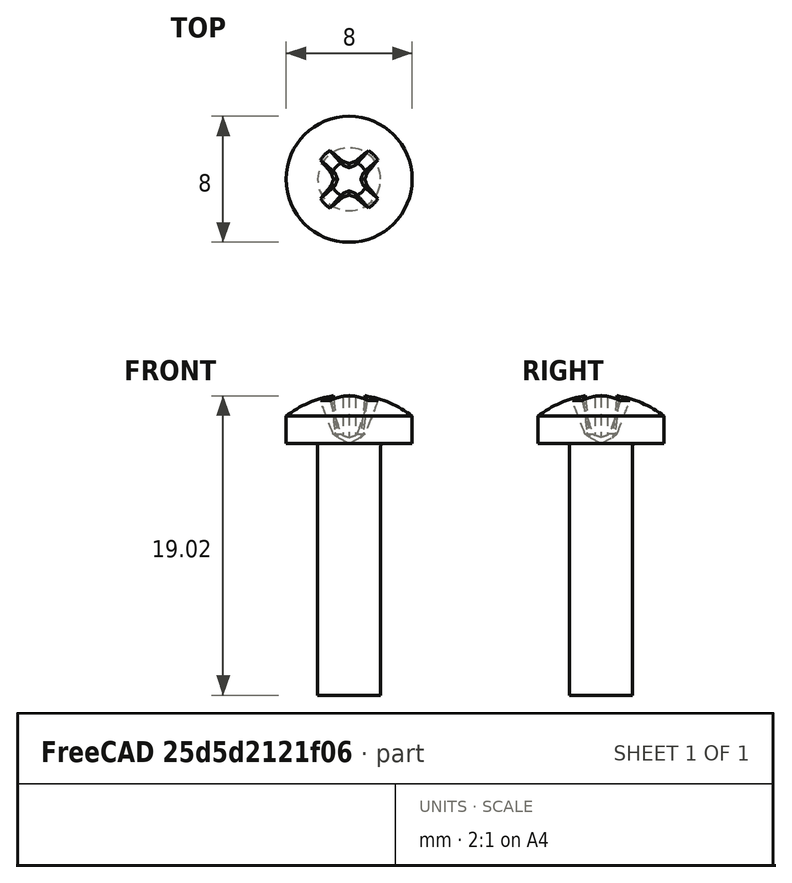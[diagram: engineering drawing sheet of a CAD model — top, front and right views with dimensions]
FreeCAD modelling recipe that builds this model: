
FCSTD DOCUMENT  (FreeCAD 0.19R24367 (Git))
Label: WheelAssembly
License: All rights reserved
LicenseURL: http://en.wikipedia.org/wiki/All_rights_reserved
objects: App::Link×5, PartDesign::CoordinateSystem×3, App::DocumentObjectGroup×3, App::Part×2, App::FeaturePython×1, Part::FeaturePython×1
note: 4 computed .brp shape members not serialized (recipe doc carries the construction recipe); baked Part::Feature solids carry a one-line shape summary decoded from their .brp
EXTERNAL_REF file=parts/Motor.FCStd obj=LCS_1
EXTERNAL_REF file=parts/Motor.FCStd obj=Motor
EXTERNAL_REF file=parts/MotorBracket.FCStd obj=LCS_1
EXTERNAL_REF file=parts/MotorBracket.FCStd obj=Front
EXTERNAL_REF file=parts/Coupling.FCStd obj=LCS_1
EXTERNAL_REF file=parts/Motor.FCStd obj=LCS_2
EXTERNAL_REF file=parts/Coupling.FCStd obj=Coupling
EXTERNAL_REF file=parts/Coupling.FCStd obj=LCS_2
EXTERNAL_REF file=parts/Wheel.FCStd obj=LCS_1
EXTERNAL_REF file=parts/Wheel.FCStd obj=Wheel
EXTERNAL_REF file=parts/Wheel.FCStd obj=LCS_2

FEATURE [PartDesign::CoordinateSystem] LCS_Origin
  AttacherType = Attacher::AttachEngine3D
  MapMode = 2
  Support = -> [X_Axis]
FEATURE [App::FeaturePython] Variables  # WARN: FeaturePython — macro-defined, semantics opaque (R4)
  Type = App::PropertyContainer
FEATURE [App::DocumentObjectGroup] Constraints
FEATURE [App::DocumentObjectGroup] Configurations
FEATURE [App::Link] Motor
  AssemblyType = Part::Link
  AttachedBy = #LCS_1
  AttachedTo = Parent Assembly#LCS_Origin
  AttachmentOffset = pos=(0,0,0) rot=(0,1,0;4.71239rad)
  LinkPlacement = pos=(22,-4.4e-15,4.9e-15) rot=(0,1,0;4.71239rad)
  LinkedObject = -> <external parts/Motor.FCStd>#Motor
  Placement = pos=(22,-4.4e-15,4.9e-15) rot=(0,1,0;4.71239rad)
  SolverId = Asm4EE
  expr: Placement = LCS_Origin.Placement * AttachmentOffset * Motor#LCS_1.Placement ^ -1
FEATURE [App::Link] Front
  AssemblyType = Part::Link
  AttachedBy = #LCS_1
  AttachedTo = Motor#LCS_1
  LinkPlacement = pos=(8,-3e-16,1.8e-15) rot=(0,0.707107,-0.707107;3.14159rad)
  LinkedObject = -> <external parts/MotorBracket.FCStd>#Front
  Placement = pos=(8,-3e-16,1.8e-15) rot=(0,0.707107,-0.707107;3.14159rad)
  SolverId = Asm4EE
  expr: Placement = Motor.Placement * Motor#LCS_1.Placement * AttachmentOffset * MotorBracket#LCS_1.Placement ^ -1
FEATURE [App::Link] Coupling
  AssemblyType = Part::Link
  AttachedBy = #LCS_1
  AttachedTo = Motor#LCS_2
  AttachmentOffset = pos=(0,0,1) rot=(0,0,1;3.14159rad)
  LinkPlacement = pos=(-7,-7,-1.6e-15) rot=(0,1,0;4.71239rad)
  LinkedObject = -> <external parts/Coupling.FCStd>#Coupling
  Placement = pos=(-7,-7,-1.6e-15) rot=(0,1,0;4.71239rad)
  SolverId = Asm4EE
  expr: Placement = Motor.Placement * Motor#LCS_2.Placement * AttachmentOffset * Coupling#LCS_1.Placement ^ -1
FEATURE [App::Link] Wheel
  AssemblyType = Part::Link
  AttachedBy = #LCS_1
  AttachedTo = Coupling#LCS_2
  LinkPlacement = pos=(-47,-7,-1.04e-14) rot=(0,1,0;4.71239rad)
  LinkedObject = -> <external parts/Wheel.FCStd>#Wheel
  Placement = pos=(-47,-7,-1.04e-14) rot=(0,1,0;4.71239rad)
  SolverId = Asm4EE
  expr: Placement = Coupling.Placement * Coupling#LCS_2.Placement * AttachmentOffset * Wheel#LCS_1.Placement ^ -1
FEATURE [Part::FeaturePython] Screw  label="M4x16-Screw"  # Fasteners workbench fastener (typed FeaturePython)
  diameter = 6
  invert = false
  length = 6
  lengthCustom = 16
  matchOuter = false
  offset = 0
  thread = false
  type = 34
FEATURE [PartDesign::CoordinateSystem] LCS_0
  AttacherType = Attacher::AttachEngine3D
  MapMode = 2
  Support = -> [X_Axis001]
FEATURE [PartDesign::CoordinateSystem] LCS_1
  AttacherType = Attacher::AttachEngine3D
  MapMode = 5
  Placement = pos=(0,0,0) rot=(0,0,1;3.14159rad)
  Support = -> [Screw]
FEATURE [App::Part] Screw001
  Group = -> [LCS_0,Screw,LCS_1]
  Origin = -> Origin001
FEATURE [App::DocumentObjectGroup] Parts
  Group = -> [Screw001]
FEATURE [App::Link] Screw001001
  AssemblyType = Part::Link
  AttachedBy = #LCS_1
  AttachedTo = Wheel#LCS_2
  LinkPlacement = pos=(-54,-7,-1.2e-14) rot=(0,1,0;4.71239rad)
  LinkedObject = -> Screw001
  Placement = pos=(-54,-7,-1.2e-14) rot=(0,1,0;4.71239rad)
  SolverId = Asm4EE
  expr: Placement = Wheel.Placement * Wheel#LCS_2.Placement * AttachmentOffset * LCS_1.Placement ^ -1
FEATURE [App::Part] Assembly  label="WheelAssembly"
  AssemblyType = Part::Link
  Group = -> [LCS_Origin,Variables,Constraints,Configurations,Motor,Front,Coupling,Wheel,Screw001001]
  Origin = -> Origin
  Type = Assembly

RESOLVED EXTERNAL PARTS (link-assembly join: the EXTERNAL_REF files above that resolve inside this repo's crawl, each included once):
---- part parts/Coupling.FCStd = doc fcstd_91e699eaf496 ----
FCSTD DOCUMENT  (FreeCAD 0.19R24367 (Git))
Label: Coupling
License: All rights reserved
LicenseURL: http://en.wikipedia.org/wiki/All_rights_reserved
objects: Sketcher::SketchObject×5, PartDesign::CoordinateSystem×3, PartDesign::Pad×2, PartDesign::Pocket×2, PartDesign::Hole×1, PartDesign::Plane×1, PartDesign::Body×1, App::Part×1
note: 20 computed .brp shape members not serialized (recipe doc carries the construction recipe); baked Part::Feature solids carry a one-line shape summary decoded from their .brp

FEATURE [PartDesign::CoordinateSystem] LCS_0
  AttacherType = Attacher::AttachEngine3D
  MapMode = 2
  Support = -> [X_Axis]
FEATURE [Sketcher::SketchObject] Sketch
  FullyConstrained = true
  MapMode = 5
  Support = -> [XY_Plane001]
  sketch-geometry (1):
    g0: Circle CenterX=0 CenterY=0 CenterZ=0 NormalX=0 NormalY=0 NormalZ=1 AngleXU=0 Radius=6
  constraints (2):
    c: Coincident(g0,g-1)
    c: Diameter(g0) = 12
FEATURE [PartDesign::Pad] Pad
  Direction = (1,1,1)
  Length = 30
  Length2 = 100
  Profile = -> Sketch
  Type = 0
FEATURE [Sketcher::SketchObject] Sketch001
  FullyConstrained = true
  MapMode = 5
  Placement = pos=(0,0,30) rot=(0,0,1;0rad)
  Support = -> [Pad]
  sketch-geometry (8):
    g0: LineSegment StartX=6.49519 StartY=-3.75 StartZ=0 EndX=6.49519 EndY=3.75 EndZ=0
    g1: LineSegment StartX=6.49519 StartY=3.75 StartZ=0 EndX=9e-16 EndY=7.5 EndZ=0
    g2: LineSegment StartX=9e-16 StartY=7.5 StartZ=0 EndX=-6.49519 EndY=3.75 EndZ=0
    g3: LineSegment StartX=-6.49519 StartY=3.75 StartZ=0 EndX=-6.49519 EndY=-3.75 EndZ=0
    g4: LineSegment StartX=-6.49519 StartY=-3.75 StartZ=0 EndX=0 EndY=-7.5 EndZ=0
    g5: LineSegment StartX=0 StartY=-7.5 StartZ=0 EndX=6.49519 EndY=-3.75 EndZ=0
    g6: Circle CenterX=0 CenterY=0 CenterZ=0 NormalX=0 NormalY=0 NormalZ=1 AngleXU=0 Radius=7.5
    g7: LineSegment StartX=0 StartY=0 StartZ=0 EndX=6.49519 EndY=0 EndZ=0
  constraints (19):
    c: Coincident(g0,g1)
    c: Coincident(g1,g2)
    c: Coincident(g2,g3)
    c: Coincident(g3,g4)
    c: Coincident(g4,g5)
    c: Coincident(g5,g0)
    c: Equal(g0, g1-g5) x5
    c: PointOnObject(g0,g6)
    c: PointOnObject(g1,g6)
    c: PointOnObject(g2,g6)
    c: PointOnObject(g3,g6)
    c: PointOnObject(g4,g6)
    c: PointOnObject(g5,g6)
    c: Coincident(g6,g-1)
    c: PointOnObject(g4,g-2)
    c: Coincident(g7,g-1)
    c: PointOnObject(g7,g-1)
    c: PointOnObject(g7,g0)
    c: Diameter(g6) = 15
FEATURE [PartDesign::Pad] Pad001
  BaseFeature = -> Pad
  Direction = (1,1,1)
  Length = 10
  Length2 = 100
  Profile = -> Sketch001
  Reversed = true
  Type = 0
FEATURE [Sketcher::SketchObject] Sketch002
  FullyConstrained = true
  MapMode = 5
  Placement = pos=(0,0,30) rot=(0,0,1;0rad)
  Support = -> [Pad001]
  sketch-geometry (1):
    g0: Circle CenterX=0 CenterY=0 CenterZ=0 NormalX=0 NormalY=0 NormalZ=1 AngleXU=0 Radius=2
  constraints (2):
    c: Coincident(g0,g-1)
    c: Diameter(g0) = 4
FEATURE [PartDesign::Hole] Hole
  BaseFeature = -> Pad001
  Depth = 5
  DepthType = 0
  Diameter = 3.5
  DrillForDepth = false
  DrillPoint = 1
  DrillPointAngle = 118
  HoleCutCountersinkAngle = 90
  HoleCutCustomValues = false
  HoleCutDepth = 0
  HoleCutDiameter = 6.1
  HoleCutType = 0
  ModelActualThread = false
  Profile = -> Sketch002
  Tapered = false
  TaperedAngle = 90
  ThreadAngle = 60
  ThreadClass = 0
  ThreadCutOffInner = 0.0541266
  ThreadCutOffOuter = 0.108253
  ThreadDirection = 0
  ThreadFit = 0
  ThreadPitch = 0.5
  ThreadSize = 11
  ThreadType = 2
  Threaded = true
FEATURE [Sketcher::SketchObject] Sketch003
  FullyConstrained = true
  MapMode = 5
  Placement = pos=(0,0,0) rot=(1,0,0;3.14159rad)
  Support = -> [Hole]
  sketch-geometry (1):
    g0: Circle CenterX=0 CenterY=0 CenterZ=0 NormalX=0 NormalY=0 NormalZ=1 AngleXU=0 Radius=3
  constraints (2):
    c: Coincident(g0,g-1)
    c: Diameter(g0) = 6
FEATURE [PartDesign::Pocket] Pocket
  BaseFeature = -> Hole
  Length = 15
  Length2 = 100
  Profile = -> Sketch003
  Type = 0
FEATURE [PartDesign::Plane] DatumPlane
  AttachmentOffset = pos=(0,6,0) rot=(1,0,0;1.5708rad)
  Length = 60
  MapMode = 45
  Placement = pos=(-1.8e-15,6,10) rot=(1,0,0;1.5708rad)
  ResizeMode = 0
  Support = -> [Pocket]
  Width = 60
FEATURE [Sketcher::SketchObject] Sketch004
  FullyConstrained = true
  MapMode = 5
  Placement = pos=(-1.8e-15,6,10) rot=(1,0,0;1.5708rad)
  Support = -> [DatumPlane]
  sketch-geometry (1):
    g0: Circle CenterX=0 CenterY=-5 CenterZ=0 NormalX=0 NormalY=0 NormalZ=1 AngleXU=0 Radius=2
  constraints (3):
    c: PointOnObject(g0,g-2)
    c: Diameter(g0) = 4
    c: DistanceY(g0,g-1) = 5
FEATURE [PartDesign::Pocket] Pocket001
  BaseFeature = -> Pocket
  Length = 5
  Length2 = 100
  Profile = -> Sketch004
  Refine = true
  Reversed = true
  Type = 0
FEATURE [PartDesign::Body] Body
  Group = -> [Sketch,Pad,Sketch001,Pad001,Sketch002,Hole,Sketch003,Pocket,DatumPlane,Sketch004,Pocket001]
  Origin = -> Origin001
  Tip = -> Pocket001
FEATURE [PartDesign::CoordinateSystem] LCS_1
  AttacherType = Attacher::AttachEngine3D
  MapMode = 5
  Placement = pos=(0,0,0) rot=(0,0,1;3.14159rad)
  Support = -> [Pocket001]
FEATURE [PartDesign::CoordinateSystem] LCS_2
  AttacherType = Attacher::AttachEngine3D
  MapMode = 5
  Placement = pos=(0,0,20) rot=(0,0,1;3.14159rad)
  Support = -> [Pocket001]
FEATURE [App::Part] Coupling
  Group = -> [LCS_0,Body,LCS_1,LCS_2]
  Origin = -> Origin
---- part parts/Motor.FCStd = doc fcstd_aef168587a4c ----
FCSTD DOCUMENT  (FreeCAD 0.19R24367 (Git))
Label: Motor
License: All rights reserved
LicenseURL: http://en.wikipedia.org/wiki/All_rights_reserved
objects: Sketcher::SketchObject×9, PartDesign::Pad×6, PartDesign::Fillet×6, PartDesign::Pocket×2, PartDesign::CoordinateSystem×2, PartDesign::PolarPattern×1, PartDesign::Chamfer×1, PartDesign::Revolution×1, PartDesign::Body×1, App::Part×1
note: 45 computed .brp shape members not serialized (recipe doc carries the construction recipe); baked Part::Feature solids carry a one-line shape summary decoded from their .brp

FEATURE [Sketcher::SketchObject] Sketch
  FullyConstrained = true
  MapMode = 5
  Support = -> [XY_Plane]
  sketch-geometry (1):
    g0: Circle CenterX=0 CenterY=0 CenterZ=0 NormalX=0 NormalY=0 NormalZ=1 AngleXU=0 Radius=18.5
  constraints (2):
    c: Coincident(g0,g-1)
    c: Diameter(g0) = 37
FEATURE [PartDesign::Pad] Pad
  Direction = (1,1,1)
  Length = 22
  Length2 = 100
  Profile = -> Sketch
  Type = 0
FEATURE [Sketcher::SketchObject] Sketch001
  FullyConstrained = true
  MapMode = 5
  Placement = pos=(0,0,22) rot=(0,0,1;0rad)
  Support = -> [Pad]
  sketch-geometry (3):
    g0: Circle CenterX=0 CenterY=0 CenterZ=0 NormalX=0 NormalY=0 NormalZ=1 AngleXU=0 Radius=15.5
    g1: LineSegment StartX=0 StartY=0 StartZ=0 EndX=7.75 EndY=13.4234 EndZ=0
    g2: Circle CenterX=7.75 CenterY=13.4234 CenterZ=0 NormalX=0 NormalY=0 NormalZ=1 AngleXU=0 Radius=1.5
  constraints (8):
    c: Coincident(g0,g-1)
    c: Diameter(g0) = 31
    c: Coincident(g1,g-1)
    c: PointOnObject(g1,g0)
    c: Distance(g1) = 15.5
    c: Angle(g1,g-2) = 0.523599
    c: Coincident(g2,g1)
    c: Diameter(g2) = 3
FEATURE [PartDesign::Pocket] Pocket
  BaseFeature = -> Pad
  Length = 5
  Length2 = 100
  Profile = -> Sketch001
  Type = 0
FEATURE [PartDesign::PolarPattern] PolarPattern
  Angle = 360
  Axis = -> Sketch001 [N_Axis]
  BaseFeature = -> Pocket
  Occurrences = 6
  Originals = -> [Pocket]
FEATURE [Sketcher::SketchObject] Sketch002
  FullyConstrained = true
  MapMode = 5
  Placement = pos=(0,0,22) rot=(0,0,1;0rad)
  Support = -> [PolarPattern]
  sketch-geometry (1):
    g0: Circle CenterX=0 CenterY=7 CenterZ=0 NormalX=0 NormalY=0 NormalZ=1 AngleXU=0 Radius=6
  constraints (3):
    c: PointOnObject(g0,g-2)
    c: Diameter(g0) = 12
    c: DistanceY(g-1,g0) = 7
FEATURE [PartDesign::Pad] Pad001
  BaseFeature = -> PolarPattern
  Direction = (1,1,1)
  Length = 6
  Length2 = 100
  Profile = -> Sketch002
  Type = 0
FEATURE [Sketcher::SketchObject] Sketch003
  FullyConstrained = true
  MapMode = 5
  Placement = pos=(0,0,28) rot=(0,0,1;0rad)
  Support = -> [Pad001]
  sketch-geometry (1):
    g0: Circle CenterX=0 CenterY=7 CenterZ=0 NormalX=0 NormalY=0 NormalZ=1 AngleXU=0 Radius=3
  constraints (3):
    c: PointOnObject(g0,g-2)
    c: Diameter(g0) = 6
    c: DistanceY(g-1,g0) = 7
FEATURE [PartDesign::Pad] Pad002
  BaseFeature = -> Pad001
  Direction = (1,1,1)
  Length = 15.5
  Length2 = 100
  Profile = -> Sketch003
  Type = 0
FEATURE [Sketcher::SketchObject] Sketch004
  FullyConstrained = true
  MapMode = 5
  Placement = pos=(0,0,43.5) rot=(0,0,1;0rad)
  Support = -> [Pad002]
  sketch-geometry (4):
    g0: LineSegment StartX=-1.7 StartY=4.5 StartZ=0 EndX=1.7 EndY=4.5 EndZ=0
    g1: LineSegment StartX=1.7 StartY=4.5 StartZ=0 EndX=1.7 EndY=4 EndZ=0
    g2: LineSegment StartX=1.7 StartY=4 StartZ=0 EndX=-1.7 EndY=4 EndZ=0
    g3: LineSegment StartX=-1.7 StartY=4 StartZ=0 EndX=-1.7 EndY=4.5 EndZ=0
  constraints (11):
    c: Coincident(g0,g1)
    c: Coincident(g1,g2)
    c: Coincident(g2,g3)
    c: Coincident(g3,g0)
    c: Horizontal(g2)
    c: Vertical(g1)
    c: Vertical(g3)
    c: Symmetric(g0,g0,g-2)
    c: Distance(g1) = 0.5
    c: DistanceY(g-1,g1) = 4
    c: Distance(g0) = 3.4
FEATURE [PartDesign::Pocket] Pocket001
  BaseFeature = -> Pad002
  Length = 12
  Length2 = 100
  Profile = -> Sketch004
  Type = 0
FEATURE [PartDesign::Fillet] Fillet
  Base = -> Pocket001 [Edge3]
  BaseFeature = -> Pocket001
  Radius = 0.5
  SupportTransform = false
FEATURE [PartDesign::Fillet] Fillet001
  Base = -> Fillet [Edge22]
  BaseFeature = -> Fillet
  Radius = 1
  SupportTransform = false
FEATURE [PartDesign::Fillet] Fillet002
  Base = -> Fillet001 [Face20]
  BaseFeature = -> Fillet001
  Radius = 0.5
  SupportTransform = false
FEATURE [PartDesign::Fillet] Fillet003
  Base = -> Fillet002 [Edge46]
  BaseFeature = -> Fillet002
  Radius = 0.5
  SupportTransform = false
FEATURE [Sketcher::SketchObject] Sketch005
  FullyConstrained = true
  MapMode = 5
  Placement = pos=(0,0,0) rot=(1,0,0;3.14159rad)
  Support = -> [Fillet003]
  sketch-geometry (1):
    g0: Circle CenterX=0 CenterY=0 CenterZ=0 NormalX=0 NormalY=0 NormalZ=1 AngleXU=0 Radius=18
  constraints (2):
    c: Coincident(g0,g-1)
    c: Diameter(g0) = 36
FEATURE [PartDesign::Pad] Pad003
  BaseFeature = -> Fillet003
  Direction = (1,1,1)
  Length = 50
  Length2 = 100
  Profile = -> Sketch005
  Type = 0
FEATURE [Sketcher::SketchObject] Sketch006
  FullyConstrained = true
  MapMode = 5
  Placement = pos=(0,0,-50) rot=(1,0,0;3.14159rad)
  Support = -> [Pad003]
  sketch-geometry (1):
    g0: Circle CenterX=0 CenterY=0 CenterZ=0 NormalX=0 NormalY=0 NormalZ=1 AngleXU=0 Radius=6.5
  constraints (2):
    c: Coincident(g0,g-1)
    c: Diameter(g0) = 13
FEATURE [PartDesign::Pad] Pad004
  BaseFeature = -> Pad003
  Direction = (1,1,1)
  Length = 4
  Length2 = 100
  Profile = -> Sketch006
  Type = 0
FEATURE [PartDesign::Chamfer] Chamfer
  Angle = 45
  Base = -> Pad004 [Edge33]
  BaseFeature = -> Pad004
  ChamferType = 0
  FlipDirection = false
  Size = 2
  Size2 = 1
  SupportTransform = false
FEATURE [Sketcher::SketchObject] Sketch007
  FullyConstrained = true
  MapMode = 5
  Placement = pos=(0,0,-54) rot=(1,0,0;3.14159rad)
  Support = -> [Chamfer]
  sketch-geometry (1):
    g0: Circle CenterX=0 CenterY=0 CenterZ=0 NormalX=0 NormalY=0 NormalZ=1 AngleXU=0 Radius=1.5
  constraints (2):
    c: Coincident(g0,g-1)
    c: Diameter(g0) = 3
FEATURE [PartDesign::Pad] Pad005
  BaseFeature = -> Chamfer
  Direction = (1,1,1)
  Length = 3
  Length2 = 100
  Profile = -> Sketch007
  Type = 0
FEATURE [PartDesign::Fillet] Fillet004
  Base = -> Pad005 [Face8]
  BaseFeature = -> Pad005
  Radius = 0.5
  SupportTransform = false
FEATURE [PartDesign::Fillet] Fillet005
  Base = -> Fillet004 [Edge11]
  BaseFeature = -> Fillet004
  Radius = 1
  SupportTransform = false
FEATURE [Sketcher::SketchObject] Sketch008
  FullyConstrained = true
  MapMode = 5
  Placement = pos=(0,0,0) rot=(1,0,0;1.5708rad)
  Support = -> [XZ_Plane]
  sketch-geometry (4):
    g0: LineSegment StartX=18 StartY=-10 StartZ=0 EndX=18.5 EndY=-10 EndZ=0
    g1: LineSegment StartX=18.5 StartY=-10 StartZ=0 EndX=18.5 EndY=-40 EndZ=0
    g2: LineSegment StartX=18.5 StartY=-40 StartZ=0 EndX=18 EndY=-40 EndZ=0
    g3: LineSegment StartX=18 StartY=-40 StartZ=0 EndX=18 EndY=-10 EndZ=0
  constraints (12):
    c: Coincident(g0,g1)
    c: Coincident(g1,g2)
    c: Coincident(g2,g3)
    c: Coincident(g3,g0)
    c: Horizontal(g0)
    c: Horizontal(g2)
    c: Vertical(g1)
    c: Vertical(g3)
    c: Distance(g2) = 0.5
    c: Distance(g1) = 30
    c: DistanceX(g-1,g2) = 18
    c: DistanceY(g0,g-1) = 10
FEATURE [PartDesign::Revolution] Revolution
  Angle = 360
  Axis = (0,2e-16,1)
  Base = (0,0,0)
  BaseFeature = -> Fillet005
  Profile = -> Sketch008
  ReferenceAxis = -> Sketch008 [V_Axis]
  Reversed = true
FEATURE [PartDesign::Body] Body
  Group = -> [Sketch,Pad,Sketch001,Pocket,PolarPattern,Sketch002,Pad001,Sketch003,Pad002,Sketch004,Pocket001,Fillet,Fillet001,Fillet002,Fillet003,Sketch005,Pad003,Sketch006,Pad004,Chamfer,Sketch007,Pad005,Fillet004,Fillet005,Sketch008,Revolution]
  Origin = -> Origin
  Placement = pos=(0,0,0) rot=(0,0,1;3.14159rad)
  Tip = -> Revolution
FEATURE [PartDesign::CoordinateSystem] LCS_1
  AttacherType = Attacher::AttachEngine3D
  MapMode = 5
  Placement = pos=(0,0,22) rot=(0,0,1;0rad)
  Support = -> [Revolution]
FEATURE [PartDesign::CoordinateSystem] LCS_2
  AttacherType = Attacher::AttachEngine3D
  AttachmentOffset = pos=(0,-7,0) rot=(0,0,1;0rad)
  MapMode = 5
  Placement = pos=(0,-7,28) rot=(0,0,1;0rad)
  Support = -> [Revolution]
FEATURE [App::Part] Motor
  Group = -> [Body,LCS_1,LCS_2]
  Origin = -> Origin001
---- part parts/MotorBracket.FCStd = doc fcstd_01f953c9f07b ----
FCSTD DOCUMENT  (FreeCAD 0.19R24367 (Git))
Label: MotorBracket
License: All rights reserved
LicenseURL: http://en.wikipedia.org/wiki/All_rights_reserved
objects: Sketcher::SketchObject×12, PartDesign::Pocket×7, PartDesign::Pad×5, PartDesign::Body×2, PartDesign::LinearPattern×1, PartDesign::CoordinateSystem×1, App::Part×1
note: 40 computed .brp shape members not serialized (recipe doc carries the construction recipe); baked Part::Feature solids carry a one-line shape summary decoded from their .brp

FEATURE [Sketcher::SketchObject] Sketch009
  FullyConstrained = true
  MapMode = 5
  Placement = pos=(0,0,0) rot=(0.57735,0.57735,0.57735;2.0944rad)
  Support = -> [YZ_Plane001]
  sketch-geometry (1):
    g0: Circle CenterX=0 CenterY=0 CenterZ=0 NormalX=0 NormalY=0 NormalZ=1 AngleXU=0 Radius=20
  constraints (2):
    c: Coincident(g0,g-1)
    c: Diameter(g0) = 40
FEATURE [PartDesign::Pad] Pad005
  Direction = (1,1,1)
  Length = 7
  Length2 = 100
  Placement = pos=(0,0,0) rot=(0.57735,0.57735,0.57735;2.0944rad)
  Profile = -> Sketch009
  Type = 0
FEATURE [Sketcher::SketchObject] Sketch010
  FullyConstrained = true
  MapMode = 5
  Placement = pos=(0,0,0) rot=(0.57735,0.57735,-0.57735;4.18879rad)
  Support = -> [Pad005]
  sketch-geometry (1):
    g0: Circle CenterX=0 CenterY=0 CenterZ=0 NormalX=0 NormalY=0 NormalZ=1 AngleXU=0 Radius=18.15
  constraints (2):
    c: Coincident(g0,g-1)
    c: Diameter(g0) = 36.3
FEATURE [PartDesign::Pocket] Pocket004
  BaseFeature = -> Pad005
  Length = 5
  Length2 = 100
  Placement = pos=(0,0,0) rot=(0.57735,0.57735,0.57735;2.0944rad)
  Profile = -> Sketch010
  Type = 0
FEATURE [Sketcher::SketchObject] Sketch011
  FullyConstrained = true
  MapMode = 5
  Placement = pos=(5,-1.1e-15,1.1e-15) rot=(0.57735,0.57735,-0.57735;4.18879rad)
  Support = -> [Pocket004]
  sketch-geometry (1):
    g0: Circle CenterX=0 CenterY=0 CenterZ=0 NormalX=0 NormalY=0 NormalZ=1 AngleXU=0 Radius=6.5
  constraints (2):
    c: Coincident(g0,g-1)
    c: Diameter(g0) = 13
FEATURE [PartDesign::Pocket] Pocket005
  BaseFeature = -> Pocket004
  Length = 5
  Length2 = 100
  Placement = pos=(0,0,0) rot=(0.57735,0.57735,0.57735;2.0944rad)
  Profile = -> Sketch011
  Type = 1
FEATURE [Sketcher::SketchObject] Sketch012
  FullyConstrained = true
  MapMode = 5
  Placement = pos=(7,-1.5e-15,1.5e-15) rot=(0.57735,0.57735,0.57735;2.0944rad)
  Support = -> [Pocket005]
  sketch-geometry (9):
    g0: LineSegment StartX=-14.5 StartY=0 StartZ=0 EndX=14.5 EndY=0 EndZ=0
    g1: LineSegment StartX=-15.5 StartY=3 StartZ=0 EndX=-13.5 EndY=3 EndZ=0
    g2: LineSegment StartX=-13.5 StartY=3 StartZ=0 EndX=-13.5 EndY=-3 EndZ=0
    g3: LineSegment StartX=-13.5 StartY=-3 StartZ=0 EndX=-15.5 EndY=-3 EndZ=0
    g4: LineSegment StartX=-15.5 StartY=-3 StartZ=0 EndX=-15.5 EndY=3 EndZ=0
    g5: LineSegment StartX=13.5 StartY=3 StartZ=0 EndX=15.5 EndY=3 EndZ=0
    g6: LineSegment StartX=15.5 StartY=3 StartZ=0 EndX=15.5 EndY=-3 EndZ=0
    g7: LineSegment StartX=15.5 StartY=-3 StartZ=0 EndX=13.5 EndY=-3 EndZ=0
    g8: LineSegment StartX=13.5 StartY=-3 StartZ=0 EndX=13.5 EndY=3 EndZ=0
  constraints (25):
    c: PointOnObject(g0,g-1)
    c: Symmetric(g0,g0,g-2)
    c: Distance(g0) = 29
    c: Coincident(g1,g2)
    c: Coincident(g2,g3)
    c: Coincident(g3,g4)
    c: Coincident(g4,g1)
    c: Horizontal(g1)
    c: Horizontal(g3)
    c: Vertical(g4)
    c: Symmetric(g1,g2,g0)
    c: Distance(g2) = 6
    c: Distance(g1) = 2
    c: DistanceX(g1,g0) = 1
    c: Coincident(g5,g6)
    c: Coincident(g6,g7)
    c: Coincident(g7,g8)
    c: Coincident(g8,g5)
    c: Horizontal(g5)
    c: Horizontal(g7)
    c: Vertical(g6)
    c: Symmetric(g5,g7,g0)
    c: Distance(g6) = 6
    c: Distance(g5) = 2
    c: DistanceX(g5,g0) = 1
FEATURE [PartDesign::Pocket] Pocket006
  BaseFeature = -> Pocket005
  Length = 5
  Length2 = 100
  Placement = pos=(0,0,0) rot=(0.57735,0.57735,0.57735;2.0944rad)
  Profile = -> Sketch012
  Type = 1
FEATURE [PartDesign::Body] Body001  label="Back"
  Group = -> [Sketch009,Pad005,Sketch010,Pocket004,Sketch011,Pocket005,Sketch012,Pocket006]
  Origin = -> Origin001
  Tip = -> Pocket006
FEATURE [Sketcher::SketchObject] Sketch016
  FullyConstrained = true
  MapMode = 5
  Placement = pos=(-46,0,-1.5e-14) rot=(0.57735,0.57735,-0.57735;4.18879rad)
  sketch-geometry (4):
    g0: LineSegment StartX=20 StartY=0 StartZ=0 EndX=-20 EndY=0 EndZ=0
    g1: LineSegment StartX=12.5 StartY=50 StartZ=0 EndX=-12.5 EndY=50 EndZ=0
    g2: LineSegment StartX=20 StartY=0 StartZ=0 EndX=12.5 EndY=50 EndZ=0
    g3: LineSegment StartX=-12.5 StartY=50 StartZ=0 EndX=-20 EndY=0 EndZ=0
  constraints (10):
    c: PointOnObject(g0,g-1)
    c: Symmetric(g0,g0,g-2)
    c: Symmetric(g1,g1,g-2)
    c: Distance(g0) = 40
    c: Distance(g1) = 25
    c: DistanceY(g1,g-1) = -50
    c: Coincident(g2,g0)
    c: Coincident(g2,g1)
    c: Coincident(g3,g1)
    c: Coincident(g3,g0)
FEATURE [Sketcher::SketchObject] Sketch018
  FullyConstrained = true
  MapMode = 5
  Placement = pos=(0,0,0) rot=(0.57735,0.57735,0.57735;2.0944rad)
  Support = -> [YZ_Plane002]
  sketch-geometry (1):
    g0: Circle CenterX=0 CenterY=0 CenterZ=0 NormalX=0 NormalY=0 NormalZ=1 AngleXU=0 Radius=20.5
  constraints (2):
    c: Coincident(g0,g-1)
    c: Diameter(g0) = 41
FEATURE [PartDesign::Pad] Pad006
  Direction = (1,1,1)
  Length = 10
  Length2 = 46
  Placement = pos=(0,0,0) rot=(0.57735,0.57735,0.57735;2.0944rad)
  Profile = -> Sketch018
  Type = 4
FEATURE [Sketcher::SketchObject] Sketch017
  FullyConstrained = true
  MapMode = 5
  Placement = pos=(-46,1.01e-14,-1.01e-14) rot=(0.57735,0.57735,-0.57735;4.18879rad)
  Support = -> [Pad006]
  sketch-geometry (1):
    g0: Circle CenterX=0 CenterY=0 CenterZ=0 NormalX=0 NormalY=0 NormalZ=1 AngleXU=0 Radius=18.75
  constraints (2):
    c: Coincident(g0,g-1)
    c: Diameter(g0) = 37.5
FEATURE [Sketcher::SketchObject] Sketch019
  FullyConstrained = true
  MapMode = 5
  Placement = pos=(10,-4e-15,3e-15) rot=(0.57735,0.57735,0.57735;2.0944rad)
  sketch-geometry (13):
    g0: LineSegment StartX=-15.5 StartY=0 StartZ=0 EndX=15.5 EndY=0 EndZ=0
    g1: LineSegment StartX=0 StartY=0 StartZ=0 EndX=0 EndY=7 EndZ=0
    g2: LineSegment StartX=-7.75 StartY=-13.4234 StartZ=0 EndX=7.75 EndY=-13.4234 EndZ=0
    g3: LineSegment StartX=-7.75 StartY=-13.4234 StartZ=0 EndX=0 EndY=0 EndZ=0
    g4: LineSegment StartX=-7.75 StartY=13.4234 StartZ=0 EndX=7.75 EndY=13.4234 EndZ=0
    g5: LineSegment StartX=-7.75 StartY=13.4234 StartZ=0 EndX=0 EndY=0 EndZ=0
    g6: Circle CenterX=0 CenterY=7 CenterZ=0 NormalX=0 NormalY=0 NormalZ=1 AngleXU=0 Radius=6.5
    g7: Circle CenterX=7.75 CenterY=-13.4234 CenterZ=0 NormalX=0 NormalY=0 NormalZ=1 AngleXU=0 Radius=1.5
    g8: Circle CenterX=15.5 CenterY=0 CenterZ=0 NormalX=0 NormalY=0 NormalZ=1 AngleXU=0 Radius=1.5
    g9: Circle CenterX=-15.5 CenterY=0 CenterZ=0 NormalX=0 NormalY=0 NormalZ=1 AngleXU=0 Radius=1.5
    g10: Circle CenterX=-7.75 CenterY=-13.4234 CenterZ=0 NormalX=0 NormalY=0 NormalZ=1 AngleXU=0 Radius=1.5
    g11: Circle CenterX=7.75 CenterY=13.4234 CenterZ=0 NormalX=0 NormalY=0 NormalZ=1 AngleXU=0 Radius=1.5
    g12: Circle CenterX=-7.75 CenterY=13.4234 CenterZ=0 NormalX=0 NormalY=0 NormalZ=1 AngleXU=0 Radius=1.5
  constraints (30):
    c: PointOnObject(g0,g-1)
    c: Symmetric(g0,g0,g-2)
    c: Distance(g0) = 31
    c: Coincident(g1,g-1)
    c: PointOnObject(g1,g-2)
    c: Distance(g1) = 7
    c: Distance(g2) = 15.5
    c: Coincident(g3,g2)
    c: Coincident(g3,g-1)
    c: Distance(g3) = 15.5
    c: Distance(g4) = 15.5
    c: Coincident(g5,g4)
    c: Coincident(g5,g-1)
    c: Distance(g5) = 15.5
    c: Coincident(g6,g1)
    c: Diameter(g6) = 13
    c: Symmetric(g2,g2,g-2)
    c: Symmetric(g4,g4,g-2)
    c: Coincident(g7,g2)
    c: Diameter(g7) = 3
    c: Coincident(g8,g0)
    c: Coincident(g9,g0)
    c: Coincident(g10,g2)
    c: Coincident(g12,g4)
    c: Coincident(g11,g4)
    c: Diameter(g12) = 3
    c: Diameter(g11) = 3
    c: Diameter(g9) = 3
    c: Diameter(g8) = 3
    c: Diameter(g10) = 3
FEATURE [PartDesign::Pocket] Pocket007
  BaseFeature = -> Pad006
  Length = 2
  Length2 = 100
  Placement = pos=(0,0,0) rot=(0.57735,0.57735,0.57735;2.0944rad)
  Profile = -> Sketch019
  Type = 0
FEATURE [Sketcher::SketchObject] Sketch013
  ExternalGeometry = -> [Pocket007]
  FullyConstrained = true
  MapMode = 5
  Support = -> [XY_Plane002]
  sketch-geometry (4):
    g0: LineSegment StartX=-46 StartY=12.5 StartZ=0 EndX=-21 EndY=12.5 EndZ=0
    g1: LineSegment StartX=-21 StartY=12.5 StartZ=0 EndX=-21 EndY=-12.5 EndZ=0
    g2: LineSegment StartX=-21 StartY=-12.5 StartZ=0 EndX=-46 EndY=-12.5 EndZ=0
    g3: LineSegment StartX=-46 StartY=-12.5 StartZ=0 EndX=-46 EndY=12.5 EndZ=0
  constraints (11):
    c: Coincident(g0,g1)
    c: Coincident(g1,g2)
    c: Coincident(g2,g3)
    c: Coincident(g3,g0)
    c: Horizontal(g0)
    c: Horizontal(g2)
    c: Vertical(g3)
    c: Distance(g0) = 25
    c: Equal(g0,g1)
    c: Symmetric(g0,g1,g-1)
    c: DistanceX(g-3,g0) = 0
FEATURE [Sketcher::SketchObject] Sketch020
  FullyConstrained = true
  MapMode = 5
  Placement = pos=(-46,1e-14,-2.5e-14) rot=(0.57735,0.57735,-0.57735;4.18879rad)
  sketch-geometry (2):
    g0: Circle CenterX=-7 CenterY=30 CenterZ=0 NormalX=0 NormalY=0 NormalZ=1 AngleXU=0 Radius=1.75
    g1: Circle CenterX=7 CenterY=30 CenterZ=0 NormalX=0 NormalY=0 NormalZ=1 AngleXU=0 Radius=1.75
  constraints (5):
    c: Diameter(g0) = 3.5
    c: Diameter(g1) = 3.5
    c: Symmetric(g0,g1,g-2)
    c: DistanceX(g0,g-1) = 7
    c: DistanceY(g-1,g0) = 30
FEATURE [PartDesign::Pad] Pad009
  BaseFeature = -> Pocket007
  Direction = (1,1,1)
  Length = 50
  Length2 = 100
  Placement = pos=(0,0,0) rot=(0.57735,0.57735,0.57735;2.0944rad)
  Profile = -> Sketch013
  Reversed = true
  Type = 0
FEATURE [PartDesign::Pad] Pad008
  BaseFeature = -> Pad009
  Direction = (1,1,1)
  Length = 2
  Length2 = 100
  Placement = pos=(0,0,0) rot=(0.57735,0.57735,0.57735;2.0944rad)
  Profile = -> Sketch016
  Reversed = true
  Type = 0
FEATURE [PartDesign::LinearPattern] LinearPattern001
  BaseFeature = -> Pad008
  Direction = -> X_Axis002
  Length = 23
  Occurrences = 2
  Originals = -> [Pad008]
  Placement = pos=(0,0,0) rot=(0.57735,0.57735,0.57735;2.0944rad)
FEATURE [PartDesign::Pocket] Pocket008
  BaseFeature = -> LinearPattern001
  Length = 54
  Length2 = 100
  Placement = pos=(0,0,0) rot=(0.57735,0.57735,0.57735;2.0944rad)
  Profile = -> Sketch017
  Type = 0
FEATURE [PartDesign::Pocket] Pocket010
  BaseFeature = -> Pocket008
  Length = 5
  Length2 = 100
  Placement = pos=(0,0,0) rot=(0.57735,0.57735,0.57735;2.0944rad)
  Profile = -> Sketch020
  Refine = true
  Type = 1
FEATURE [Sketcher::SketchObject] Sketch021
  ExternalGeometry = -> [Pocket010]
  FullyConstrained = true
  MapMode = 5
  Placement = pos=(0,0,0) rot=(1,0,0;1.5708rad)
  Support = -> [XZ_Plane002]
  sketch-geometry (3):
    g0: LineSegment StartX=7 StartY=-20 StartZ=0 EndX=-21 EndY=-20 EndZ=0
    g1: LineSegment StartX=-21 StartY=-20 StartZ=0 EndX=-21 EndY=-50 EndZ=0
    g2: LineSegment StartX=-21 StartY=-50 StartZ=0 EndX=7 EndY=-20 EndZ=0
  constraints (8):
    c: Horizontal(g0)
    c: Coincident(g1,g0)
    c: Vertical(g1)
    c: Coincident(g2,g1)
    c: Coincident(g2,g0)
    c: Distance(g0) = 28
    c: Distance(g1) = 30
    c: Coincident(g1,g-3)
FEATURE [PartDesign::Pad] Pad010
  BaseFeature = -> Pocket010
  Direction = (1,1,1)
  Length = 3
  Length2 = 100
  Midplane = true
  Placement = pos=(0,0,0) rot=(0.57735,0.57735,0.57735;2.0944rad)
  Profile = -> Sketch021
  Type = 0
FEATURE [Sketcher::SketchObject] Sketch022
  ExternalGeometry = -> [Pad010]
  FullyConstrained = true
  MapMode = 5
  Placement = pos=(0,0,-50) rot=(0.707107,0.707107,0;3.14159rad)
  Support = -> [Pad010]
  sketch-geometry (4):
    g0: LineSegment StartX=-10.5 StartY=-23 StartZ=0 EndX=10.5 EndY=-23 EndZ=0
    g1: LineSegment StartX=10.5 StartY=-23 StartZ=0 EndX=10.5 EndY=-44 EndZ=0
    g2: LineSegment StartX=10.5 StartY=-44 StartZ=0 EndX=-10.5 EndY=-44 EndZ=0
    g3: LineSegment StartX=-10.5 StartY=-44 StartZ=0 EndX=-10.5 EndY=-23 EndZ=0
  constraints (11):
    c: Coincident(g0,g1)
    c: Coincident(g1,g2)
    c: Coincident(g2,g3)
    c: Coincident(g3,g0)
    c: Horizontal(g2)
    c: Vertical(g1)
    c: Vertical(g3)
    c: Symmetric(g0,g0,g-2)
    c: Equal(g0,g1)
    c: Distance(g0) = 21
    c: DistanceY(g0,g-3) = 2
FEATURE [PartDesign::Pocket] Pocket011
  BaseFeature = -> Pad010
  Length = 29
  Length2 = 100
  Placement = pos=(0,0,0) rot=(0.57735,0.57735,0.57735;2.0944rad)
  Profile = -> Sketch022
  Type = 0
FEATURE [PartDesign::Body] Body002  label="Body"
  Group = -> [Sketch018,Sketch019,Pad006,Sketch017,Pocket007,Sketch013,Pad009,Sketch016,Pad008,LinearPattern001,Pocket008,Sketch020,Pocket010,Sketch021,Pad010,Sketch022,Pocket011]
  Origin = -> Origin002
  Tip = -> Pocket011
FEATURE [PartDesign::CoordinateSystem] LCS_1
  AttacherType = Attacher::AttachEngine3D
  MapMode = 5
  Placement = pos=(8,-3e-15,1.8e-15) rot=(0.57735,-0.57735,0.57735;4.18879rad)
  Support = -> [Pocket011]
FEATURE [App::Part] Front
  Group = -> [Body002,LCS_1]
  Origin = -> Origin
---- part parts/Wheel.FCStd = doc fcstd_764c865fbecf ----
FCSTD DOCUMENT  (FreeCAD 0.19R24367 (Git))
Label: Wheel
License: All rights reserved
LicenseURL: http://en.wikipedia.org/wiki/All_rights_reserved
objects: Sketcher::SketchObject×8, PartDesign::CoordinateSystem×3, PartDesign::Pocket×3, PartDesign::Body×2, Part::FeaturePython×2, PartDesign::AdditivePipe×1, PartDesign::Revolution×1, PartDesign::PolarPattern×1, PartDesign::Pad×1, App::Part×1
note: 27 computed .brp shape members not serialized (recipe doc carries the construction recipe); baked Part::Feature solids carry a one-line shape summary decoded from their .brp

FEATURE [PartDesign::CoordinateSystem] LCS_0
  AttacherType = Attacher::AttachEngine3D
  MapMode = 2
  Support = -> [X_Axis]
FEATURE [Sketcher::SketchObject] Sketch
  FullyConstrained = true
  MapMode = 5
  Placement = pos=(0,0,0) rot=(1,0,0;1.5708rad)
  Support = -> [XZ_Plane001]
  sketch-geometry (4):
    g0: ArcOfCircle CenterX=-50 CenterY=30 CenterZ=0 NormalX=0 NormalY=0 NormalZ=1 AngleXU=0 Radius=15 StartAngle=3e-16 EndAngle=3.14159
    g1: ArcOfCircle CenterX=-50 CenterY=-30 CenterZ=0 NormalX=0 NormalY=0 NormalZ=1 AngleXU=0 Radius=15 StartAngle=3.14159 EndAngle=6.28319
    g2: LineSegment StartX=-65 StartY=30 StartZ=0 EndX=-65 EndY=-30 EndZ=0
    g3: LineSegment StartX=-35 StartY=30 StartZ=0 EndX=-35 EndY=-30 EndZ=0
  constraints (9):
    c: Tangent(g0,g3) = 1.5708
    c: Tangent(g0,g2) = -1.5708
    c: Tangent(g2,g1) = -1.5708
    c: Tangent(g3,g1) = 1.5708
    c: Vertical(g2)
    c: Symmetric(g0,g1,g-1)
    c: Distance(g3) = 60
    c: DistanceX(g0,g-1) = 65
    c: DistanceX(g0,g0) = 30
FEATURE [Sketcher::SketchObject] Sketch001
  FullyConstrained = true
  MapMode = 5
  Support = -> [XY_Plane001]
  sketch-geometry (1):
    g0: Circle CenterX=0 CenterY=0 CenterZ=0 NormalX=0 NormalY=0 NormalZ=1 AngleXU=0 Radius=65
  constraints (2):
    c: Coincident(g0,g-1)
    c: Diameter(g0) = 130
FEATURE [PartDesign::AdditivePipe] AdditivePipe
  AuxilleryCurvelinear = true
  AuxillerySpineTangent = false
  Binormal = (0,0,0)
  Mode = 0
  Placement = pos=(0,0,0) rot=(1,0,0;1.5708rad)
  Profile = -> Sketch
  Spine = -> Sketch001
  SpineTangent = false
  Transformation = 0
  Transition = 0
FEATURE [PartDesign::Body] Body  label="Tire"
  Group = -> [Sketch,Sketch001,AdditivePipe]
  Origin = -> Origin001
  Tip = -> AdditivePipe
FEATURE [Sketcher::SketchObject] Mapped_Sketch
  FullyConstrained = false
  sketch-geometry (14):
    g0: LineSegment StartX=0 StartY=-60 StartZ=0 EndX=34.0339 EndY=-60 EndZ=0
    g1: LineSegment StartX=34.0339 StartY=-60 StartZ=0 EndX=34.0339 EndY=0 EndZ=0
    g2: LineSegment StartX=34.0339 StartY=0 StartZ=0 EndX=0 EndY=0 EndZ=0
    g3: LineSegment StartX=0 StartY=0 StartZ=0 EndX=0 EndY=-60 EndZ=0
    g4: LineSegment StartX=-15.8351 StartY=-30 StartZ=0 EndX=56.2328 EndY=-30 EndZ=0
    g5: LineSegment StartX=17.017 StartY=5.62699 StartZ=0 EndX=17.017 EndY=-66.3234 EndZ=0
    g6: LineSegment StartX=24.517 StartY=-58.2653 StartZ=0 EndX=24.517 EndY=-32.2845 EndZ=0
    g7: LineSegment StartX=24.517 StartY=-32.2845 StartZ=0 EndX=2.01696 EndY=-45.2749 EndZ=0
    g8: LineSegment StartX=2.01696 StartY=-45.2749 StartZ=0 EndX=24.517 EndY=-58.2653 EndZ=0
    g9: Circle CenterX=17.017 CenterY=-45.2749 CenterZ=0 NormalX=0 NormalY=0 NormalZ=1 AngleXU=0 Radius=15
    g10: LineSegment StartX=32.017 StartY=-15.1256 StartZ=0 EndX=9.51696 EndY=-2.1352 EndZ=0
    g11: LineSegment StartX=9.51696 StartY=-2.1352 StartZ=0 EndX=9.51696 EndY=-28.116 EndZ=0
    g12: LineSegment StartX=9.51696 StartY=-28.116 StartZ=0 EndX=32.017 EndY=-15.1256 EndZ=0
    g13: Circle CenterX=17.017 CenterY=-15.1256 CenterZ=0 NormalX=0 NormalY=0 NormalZ=1 AngleXU=0 Radius=15
  constraints (36):
    c: Coincident(g0,g1)
    c: Coincident(g1,g2)
    c: Coincident(g2,g3)
    c: Coincident(g3,g0)
    c: Horizontal(g0)
    c: Horizontal(g2)
    c: Vertical(g1)
    c: Vertical(g3)
    c: DistanceX(g2,g2) = 34.0339
    c: DistanceY(g1,g1) = 60
    c: DistanceX(g0,g-1) = 0
    c: DistanceY(g0,g-1) = 60
    c: Symmetric(g1,g0,g4)
    c: Symmetric(g-1,g1,g5)
    c: Coincident(g6,g7)
    c: Coincident(g7,g8)
    c: Coincident(g8,g6)
    c: Equal(g6,g7)
    c: Equal(g6,g8)
    c: PointOnObject(g6,g9)
    c: PointOnObject(g7,g9)
    c: PointOnObject(g8,g9)
    c: PointOnObject(g9,g5)
    c: Parallel(g6,g5)
    c: Diameter(g9) = 30
    c: Coincident(g10,g11)
    c: Coincident(g11,g12)
    c: Coincident(g12,g10)
    c: Equal(g10,g11)
    c: Equal(g10,g12)
    c: PointOnObject(g10,g13)
    c: PointOnObject(g11,g13)
    c: PointOnObject(g12,g13)
    c: PointOnObject(g13,g5)
    c: Diameter(g13) = 30
    c: Parallel(g11,g5)
FEATURE [Part::FeaturePython] Sketch_On_Surface  # WARN: FeaturePython — macro-defined, semantics opaque (R4)
  ConstructionBounds = true
  FillExtrusion = true
  FillFaces = true
  ReverseU = false
  ReverseV = false
  Sketch = -> Mapped_Sketch
  SwapUV = false
  Thickness = 3
FEATURE [Part::FeaturePython] Array  # Draft array (typed FeaturePython)
  Angle = 360
  ArrayType = 1
  Axis = (0,0,1)
  Base = -> Sketch_On_Surface
  Center = (0,0,0)
  Count = 24
  ExpandArray = false
  Fuse = false
  IntervalAxis = (0,0,0)
  IntervalX = (50,0,0)
  IntervalY = (0,50,0)
  IntervalZ = (0,0,50)
  NumberCircles = 3
  NumberPolar = 24
  NumberX = 2
  NumberY = 2
  NumberZ = 1
  PlacementList = 24 placements: [(0,0,0),(0,0,0),(0,0,0),(0,0,0),(0,0,0),(0,0,0),(0,0,0),(0,0,0),(0,0,0),(0,0,0),(0,0,0),(0,0,0),(0,0,0),(0,0,0),(0,0,0),(0,0,0),(0,0,0),(0,0,0),(0,0,0),(0,0,0),(0,0,0),(0,0,0),(0,0,0),(0,0,0)]
  RadialDistance = 50
  ScaleList = (24) [(1,1,1),(1,1,1),(1,1,1),(1,1,1),(1,1,1),(1,1,1),(1,1,1),(1,1,1),(1,1,1),(1,1,1),(1,1,1),(1,1,1),(1,1,1),(1,1,1),(1,1,1),(1,1,1),(1,1,1),(1,1,1),+6 more]
  Symmetry = 1
  TangentialDistance = 25
FEATURE [Sketcher::SketchObject] Sketch004
  FullyConstrained = false
  MapMode = 5
  Placement = pos=(0,0,0) rot=(1,0,0;1.5708rad)
  Support = -> [XZ_Plane002]
  sketch-geometry (13):
    g0: LineSegment StartX=0 StartY=0 StartZ=0 EndX=0 EndY=7 EndZ=0
    g1: LineSegment StartX=0 StartY=7 StartZ=0 EndX=5 EndY=7 EndZ=0
    g2: LineSegment StartX=35 StartY=30 StartZ=0 EndX=35 EndY=-30 EndZ=0
    g3: LineSegment StartX=35 StartY=30 StartZ=0 EndX=32 EndY=30 EndZ=0
    g4: Circle CenterX=5 CenterY=7 CenterZ=0 NormalX=0 NormalY=0 NormalZ=1 AngleXU=0 Radius=1
    g5: Circle CenterX=20.9877 CenterY=16.6642 CenterZ=0 NormalX=0 NormalY=0 NormalZ=1 AngleXU=0 Radius=1
    g6: Circle CenterX=32 CenterY=30 CenterZ=0 NormalX=0 NormalY=0 NormalZ=1 AngleXU=0 Radius=1
    g7: BSplineCurve PolesCount=3 KnotsCount=2 Degree=2 IsPeriodic=0
    g8: GeomPoint X=5 Y=7 Z=0
    g9: GeomPoint X=32 Y=30 Z=0
    g10: LineSegment StartX=35 StartY=-30 StartZ=0 EndX=32 EndY=-30 EndZ=0
    g11: LineSegment StartX=32 StartY=-30 StartZ=0 EndX=32 EndY=0 EndZ=0
    g12: LineSegment StartX=0 StartY=0 StartZ=0 EndX=32 EndY=0 EndZ=0
  constraints (31):
    c: Coincident(g0,g-1)
    c: PointOnObject(g0,g-2)
    c: Coincident(g1,g0)
    c: Horizontal(g1)
    c: Coincident(g3,g2)
    c: Horizontal(g3)
    c: Coincident(g7,g1)
    c: Weight(g4) = 1
    c: Equal(g4,g5)
    c: Equal(g4,g6)
    c: Coincident(g7,g3)
    c: InternalAlignment(g4,g7)
    c: InternalAlignment(g5,g7)
    c: InternalAlignment(g6,g7)
    c: InternalAlignment(g8,g7)
    c: InternalAlignment(g9,g7)
    c: Distance(g0) = 7
    c: Distance(g1) = 5
    c: Distance(g2) = 60
    c: Distance(g3) = 3
    c: DistanceX(g0,g2) = 35
    c: Symmetric(g2,g2,g-1)
    c: Coincident(g10,g2)
    c: Horizontal(g10)
    c: Distance(g10) = 3
    c: Coincident(g11,g10)
    c: PointOnObject(g11,g-1)
    c: Vertical(g11)
    c: Coincident(g12,g11)
    c: Horizontal(g12)
    c: Distance(g12) = 32
FEATURE [PartDesign::Revolution] Revolution
  Angle = 360
  Axis = (0,-2e-16,1)
  Base = (0,0,0)
  Midplane = true
  Placement = pos=(0,0,0) rot=(1,0,0;1.5708rad)
  Profile = -> Sketch004
  ReferenceAxis = -> Sketch004 [V_Axis]
  Reversed = true
FEATURE [Sketcher::SketchObject] Sketch006
  FullyConstrained = true
  MapMode = 5
  Support = -> [XY_Plane002]
  sketch-geometry (1):
    g0: Circle CenterX=0 CenterY=20 CenterZ=0 NormalX=0 NormalY=0 NormalZ=1 AngleXU=0 Radius=10
  constraints (3):
    c: PointOnObject(g0,g-2)
    c: Diameter(g0) = 20
    c: DistanceY(g-1,g0) = 20
FEATURE [PartDesign::Pocket] Pocket
  BaseFeature = -> Revolution
  Length = 5
  Length2 = 100
  Placement = pos=(0,0,0) rot=(1,0,0;1.5708rad)
  Profile = -> Sketch006
  Reversed = true
  Type = 1
FEATURE [PartDesign::PolarPattern] PolarPattern
  Angle = 360
  Axis = -> Sketch006 [N_Axis]
  BaseFeature = -> Pocket
  Occurrences = 5
  Originals = -> [Pocket]
  Placement = pos=(0,0,0) rot=(1,0,0;1.5708rad)
FEATURE [Sketcher::SketchObject] Sketch007
  FullyConstrained = true
  MapMode = 5
  Support = -> [XY_Plane002]
  sketch-geometry (1):
    g0: Circle CenterX=0 CenterY=0 CenterZ=0 NormalX=0 NormalY=0 NormalZ=1 AngleXU=0 Radius=9
  constraints (2):
    c: Coincident(g0,g-1)
    c: Diameter(g0) = 18
FEATURE [PartDesign::Pad] Pad
  BaseFeature = -> PolarPattern
  Direction = (1,1,1)
  Length = 20
  Length2 = 100
  Placement = pos=(0,0,0) rot=(1,0,0;1.5708rad)
  Profile = -> Sketch007
  Reversed = true
  Type = 0
FEATURE [Sketcher::SketchObject] Sketch008
  FullyConstrained = true
  MapMode = 5
  Placement = pos=(0,0,-20) rot=(1,0,0;3.14159rad)
  Support = -> [Pad]
  sketch-geometry (7):
    g0: LineSegment StartX=6.49519 StartY=-3.75 StartZ=0 EndX=6.49519 EndY=3.75 EndZ=0
    g1: LineSegment StartX=6.49519 StartY=3.75 StartZ=0 EndX=0 EndY=7.5 EndZ=0
    g2: LineSegment StartX=0 StartY=7.5 StartZ=0 EndX=-6.49519 EndY=3.75 EndZ=0
    g3: LineSegment StartX=-6.49519 StartY=3.75 StartZ=0 EndX=-6.49519 EndY=-3.75 EndZ=0
    g4: LineSegment StartX=-6.49519 StartY=-3.75 StartZ=0 EndX=0 EndY=-7.5 EndZ=0
    g5: LineSegment StartX=0 StartY=-7.5 StartZ=0 EndX=6.49519 EndY=-3.75 EndZ=0
    g6: Circle CenterX=0 CenterY=0 CenterZ=0 NormalX=0 NormalY=0 NormalZ=1 AngleXU=0 Radius=7.5
  constraints (16):
    c: Coincident(g0,g1)
    c: Coincident(g1,g2)
    c: Coincident(g2,g3)
    c: Coincident(g3,g4)
    c: Coincident(g4,g5)
    c: Coincident(g5,g0)
    c: Equal(g0, g1-g5) x5
    c: PointOnObject(g0,g6)
    c: PointOnObject(g1,g6)
    c: PointOnObject(g2,g6)
    c: PointOnObject(g3,g6)
    c: PointOnObject(g4,g6)
    c: PointOnObject(g5,g6)
    c: Coincident(g6,g-1)
    c: PointOnObject(g4,g-2)
    c: Diameter(g6) = 15
FEATURE [PartDesign::Pocket] Pocket001
  BaseFeature = -> Pad
  Length = 5
  Length2 = 100
  Placement = pos=(0,0,0) rot=(1,0,0;1.5708rad)
  Profile = -> Sketch008
  Type = 0
FEATURE [Sketcher::SketchObject] Sketch009
  FullyConstrained = true
  MapMode = 5
  Placement = pos=(0,0,7) rot=(0,0,1;3.14159rad)
  Support = -> [Pocket001]
  sketch-geometry (1):
    g0: Circle CenterX=0 CenterY=0 CenterZ=0 NormalX=0 NormalY=0 NormalZ=1 AngleXU=0 Radius=2
  constraints (2):
    c: Coincident(g0,g-1)
    c: Diameter(g0) = 4
FEATURE [PartDesign::Pocket] Pocket002
  BaseFeature = -> Pocket001
  Length = 5
  Length2 = 100
  Placement = pos=(0,0,0) rot=(1,0,0;1.5708rad)
  Profile = -> Sketch009
  Type = 1
FEATURE [PartDesign::Body] Body002  label="Rim"
  Group = -> [Sketch004,Revolution,Sketch006,Pocket,PolarPattern,Sketch007,Pad,Sketch008,Pocket001,Sketch009,Pocket002]
  Origin = -> Origin002
  Tip = -> Pocket002
FEATURE [PartDesign::CoordinateSystem] LCS_1
  AttacherType = Attacher::AttachEngine3D
  MapMode = 5
  Placement = pos=(0,0,-20) rot=(0,0,1;3.14159rad)
  Support = -> [Pocket002]
FEATURE [PartDesign::CoordinateSystem] LCS_2
  AttacherType = Attacher::AttachEngine3D
  MapMode = 5
  Placement = pos=(0,0,7) rot=(0,0,1;3.14159rad)
  Support = -> [Pocket002]
FEATURE [App::Part] Wheel
  Group = -> [LCS_0,Body,Mapped_Sketch,Sketch_On_Surface,Array,Body002,LCS_1,LCS_2]
  Origin = -> Origin
